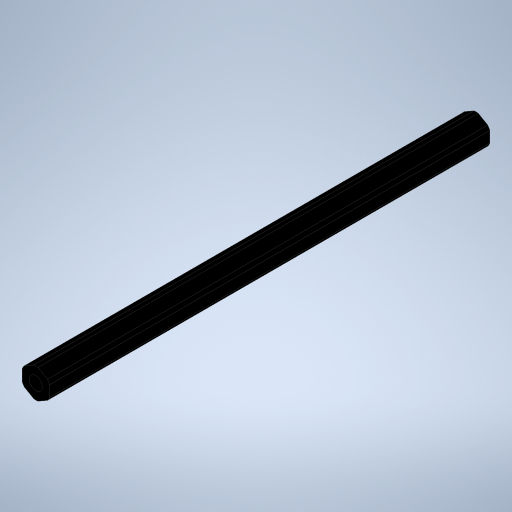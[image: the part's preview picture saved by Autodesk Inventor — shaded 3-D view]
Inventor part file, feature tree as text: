
AUTODESK INVENTOR PART (.ipt)
format: ipt  version: 2023.4 (Build 274418000, 418)  size: 265,216 bytes
history: native  units: in
note: dims shown in document units (in); Inventor stores cm internally (conversion verified against a paired STEP export)
features: extrude x2, projected_geometry x2, hole x1
ambient origin geometry x8: Origin, YZ Plane, XZ Plane, XY Plane, X Axis, Y Axis, Z Axis, Center Point
bodies: Solid1 (feature_tree)
feature tree (5):
  extrude  "Extrusion1"  TaperAngle=0.0deg  [1 undecoded]
  hole  "Hole1"  [1 undecoded]
  extrude  "Extrusion3"  TaperAngle=0.0deg  [1 undecoded]
  projected_geometry  "Project Cut Edges1"
  projected_geometry  "Project Cut Edges2"
note: 3 required parameter values undecoded (feature->parameter linkage not recoverable at this tier; creation-order binding heuristic only, values carry confidence <= 0.55)
